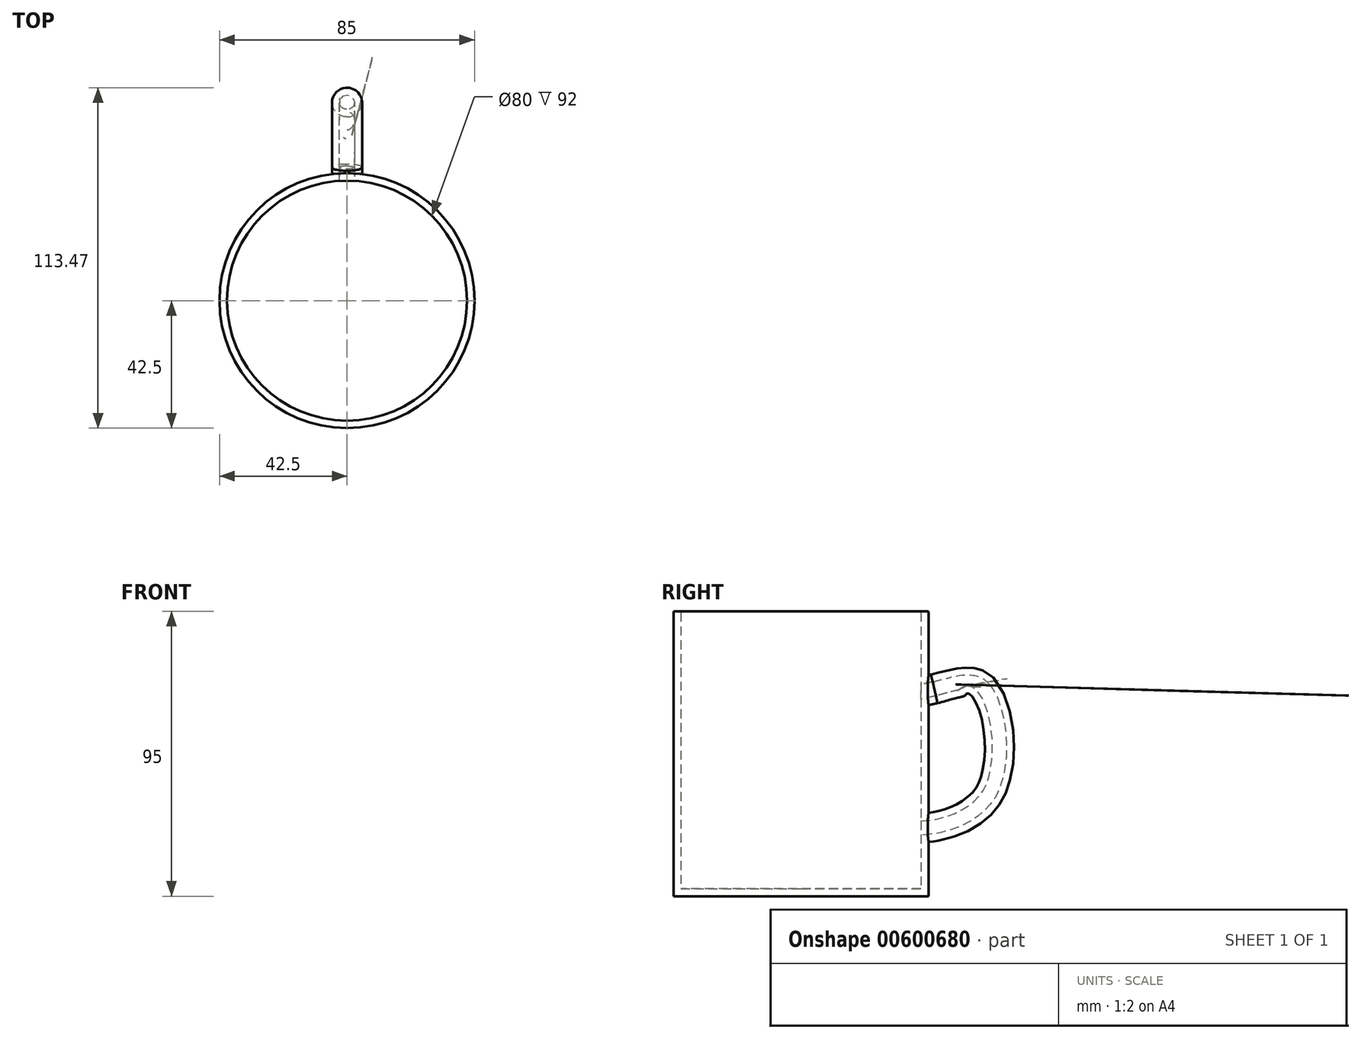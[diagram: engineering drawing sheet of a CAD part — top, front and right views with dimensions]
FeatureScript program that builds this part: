
annotation { "Feature Type Name" : "Feature", "Feature Type Description" : "" }
export const myFeature = defineFeature(function(context is Context, id is Id, definition is map)
    precondition{}
    {
        {
            var Q0;
            Q0=qCreatedBy(makeId("Top.planeOp"),FACE);
            var sketch = newSketch(context, id + "F0", { "sketchPlane" : qUnion([Q0])});
            skCircle(sketch, "E0", {"center": v(0, 0) * mm, "radius": 42.5 * mm});
            skSolve(sketch);
        }
        {
            var Q0;
            Q0 = qSketchRegion(id + "F0", true);
            extrude(context, id + "F1", {"entities" : qUnion([Q0]), "depth" : 95 * mm, "offsetDistance" : 25 * mm});
        }
        {
            var Q0;
            Q0=qCreatedBy(makeId("Front.planeOp"),FACE);
            cPlane(context, id + "F2", {"entities" : qUnion([Q0]), "cplaneType" : CPlaneType.OFFSET, "offset" : 42.5 * mm, "oppositeDirection" : true, "width" : 150 * mm, "height" : 150 * mm});
        }
        {
            var Q0;
            Q0=qCreatedBy(makeId("Right.planeOp"),FACE);
            var sketch = newSketch(context, id + "F3", { "sketchPlane" : qUnion([Q0])});
            skFitSpline(sketch, "E1", {"points": [v(43.13, 74.43) * mm, v(64.22, 73.58) * mm, v(68.27, 33.11) * mm, v(45.05, 17.77) * mm, v(33.12, 17.77) * mm], "startDerivative": vector(101.22, 27.52) * mm, "endDerivative": vector(-60.03, 6.83) * mm});
            skFitSpline(sketch, "E2", {"points": [v(43.13, 74.43) * mm, v(33.12, 71.67) * mm, v(28.44, 68.68) * mm], "startDerivative": vector(-19.13, -4.14) * mm, "endDerivative": vector(-9.78, -7.54) * mm});
            skSolve(sketch);
        }
        {
            var Q0;
            Q0=qCreatedBy(id+"F2.planeOp",FACE);
            var sketch = newSketch(context, id + "F4", { "sketchPlane" : qUnion([Q0])});
            skCircle(sketch, "E3", {"center": v(0, 68.68) * mm, "radius": 5 * mm});
            skSolve(sketch);
        }
        {
            var Q0;
            Q0 = qSketchRegion(id + "F4", true);
            var Q1;
            Q1 = qConstructionFilter(qBodyType(qCreatedBy(id + "F3" ,EDGE), BodyType.WIRE), ConstructionObject.NO);
            sweep(context, id + "F5", {"operationType" : NewBodyOperationType.ADD, "profiles" : qUnion([Q0]), "path" : qUnion([Q1])});
        }
        {
            var Q0;
            Q0=makeQuery(id+"F1.opExtrude","CAP_FACE",FACE,{"disambiguationData":[OSD([sQuery(id+"F0.wireOp",EDGE,"E0")])],"isStart":false});
            shell(context, id + "F6", {"entities" : qUnion([Q0]), "thickness" : 2.5 * mm});
        }
        {
            var Q0;
            {var subQ0=sQuery(id+"F0.wireOp",EDGE,"E0");Q0=makeQuery(id+"F6.opShell","OFFSET_EDGE",EDGE,{"disambiguationData":[OSD([subQ0]),TDD([makeQuery(id+"F1.opExtrude","CAP_EDGE",EDGE,{"disambiguationData":[OSD([subQ0])],"isStart":false})])]});}
            var Q1;
            Q1=makeQuery(id+"F1.opExtrude","CAP_EDGE",EDGE,{"disambiguationData":[OSD([sQuery(id+"F0.wireOp",EDGE,"E0")])],"isStart":false});
            fillet(context, id + "F7", {"entities" : qUnion([Q0, Q1]), "radius" : 0.5 * mm, "tangentPropagation" : true, "allowEdgeOverflow" : false});
        }
    });
